SOLIDWORKS PART (.sldprt)
format: sldprt  version: not decoded by parser v0  size: 221,696 bytes
history: native  units: mm
features: sketch x6, cut_extrude x4, plane x3, extrude x2, material x1 (+10 scaffold rows collapsed)
feature tree (26):
  scaffold x10  (default folders/planes/origin — collapsed)
  material  "Matériau <non spécifié>"
  plane  "Plan de face"
  plane  "Plan de dessus"
  plane  "Plan de droite"
  sketch  "Esquisse1"  dims[D1=20.0mm D2=20.0mm D3=40.0mm D4=10.0mm]
  extrude  "Boss.-Extru.1"  Depth=30mm
  sketch  "Esquisse3"  dims[D1=0.5mm]
  cut_extrude  "Enlèv. mat.-Extru.1"  Depth=30mm
  sketch  "Esquisse4"  dims[D1=~1.291769mm]
  cut_extrude  "Enlèv. mat.-Extru.2"  [1 undecoded]
  sketch  "Esquisse5"  dims[D1=~2.406682mm]
  cut_extrude  "Enlèv. mat.-Extru.3"  [1 undecoded]
  sketch  "Esquisse6"  dims[D1=15.0mm D2=15.0mm D3=8.0mm D4=12.0mm D5=23.0mm D6=27.0mm D7=23.0mm D8=23.0mm]
  extrude  "Boss.-Extru.2"  Depth=10mm
  sketch  "Esquisse7"  dims[D1=~3.388632mm]
  cut_extrude  "Enlèv. mat.-Extru.4"  [1 undecoded]
decode coverage: 9 of 12 modeling features carry decoded parameters
note: ~ marks probable driven/reference dimensions
note: 3 parameter values undecoded
summary: no parameter record found for 3 features
note: suppression state not decoded; provenance and decode notes live in map.json
